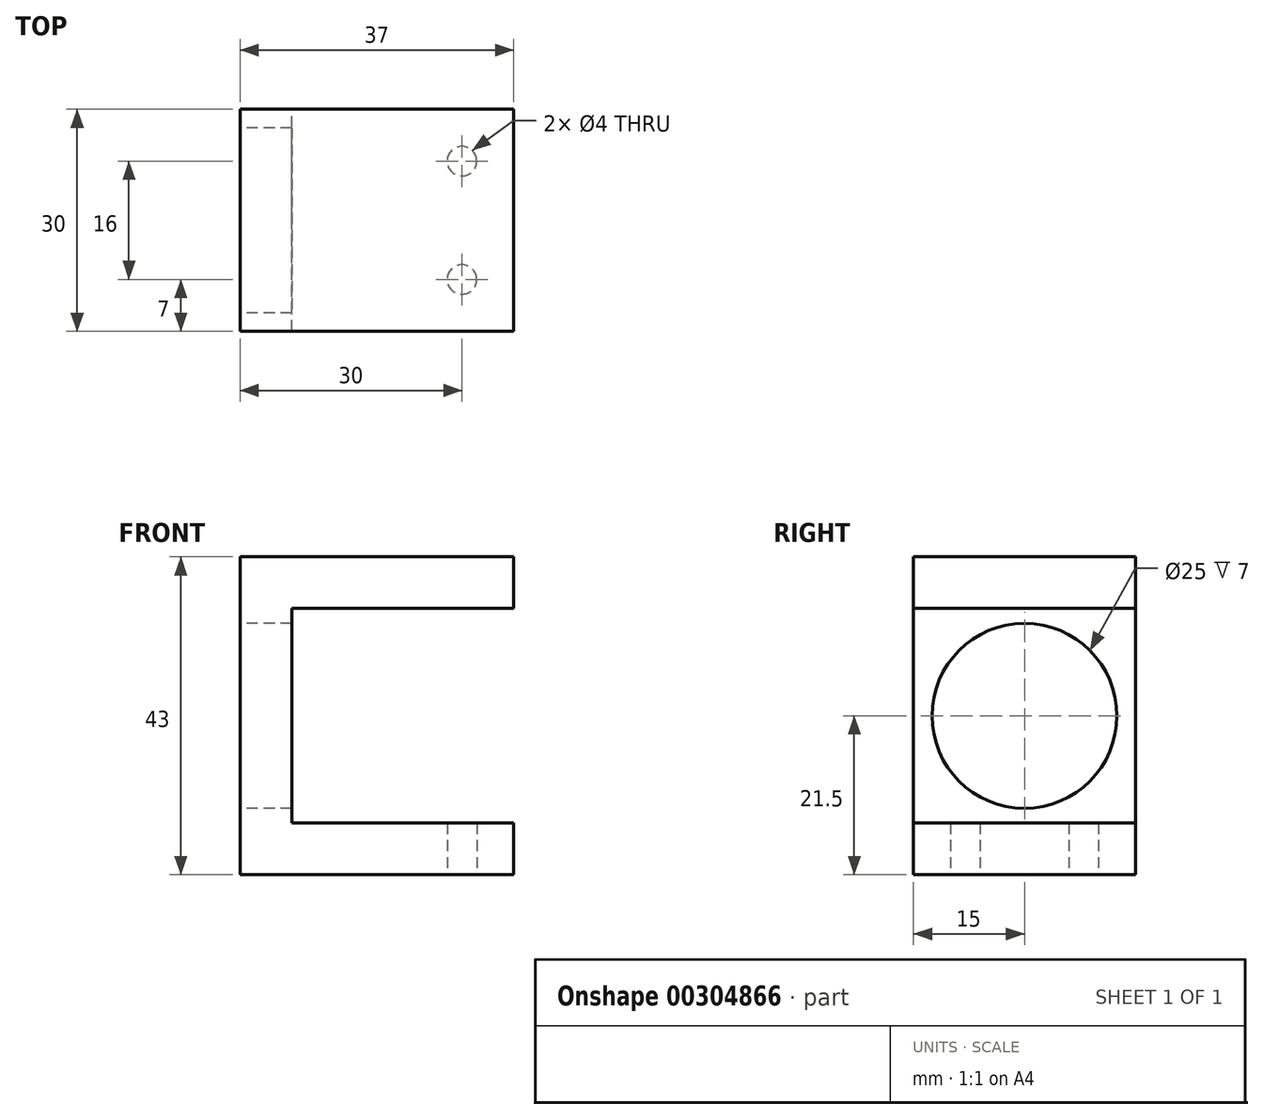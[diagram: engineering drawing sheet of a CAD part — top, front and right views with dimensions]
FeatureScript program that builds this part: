
annotation { "Feature Type Name" : "Feature", "Feature Type Description" : "" }
export const myFeature = defineFeature(function(context is Context, id is Id, definition is map)
    precondition{}
    {
        {
            var Q0;
            Q0=qCreatedBy(makeId("Front.planeOp"),FACE);
            var sketch = newSketch(context, id + "F0", { "sketchPlane" : qUnion([Q0])});
            skLineSegment(sketch, "E0.bottom", {"start": v(15, -14.5) * mm, "end": v(-15, -14.5) * mm});
            skLineSegment(sketch, "E0.top", {"start": v(15, 14.5) * mm, "end": v(-15, 14.5) * mm});
            skLineSegment(sketch, "E0.left", {"start": v(15, -14.5) * mm, "end": v(15, 14.5) * mm});
            skLineSegment(sketch, "E0.right", {"start": v(-15, -14.5) * mm, "end": v(-15, 14.5) * mm});
            skPoint(sketch, "E0.middle", {"position": v(0, 0) * mm});
            skLineSegment(sketch, "E1.0", {"start": v(22, 21.5) * mm, "end": v(-22, 21.5) * mm});
            skLineSegment(sketch, "E1.1", {"start": v(22, -21.5) * mm, "end": v(22, 21.5) * mm});
            skLineSegment(sketch, "E1.2", {"start": v(22, -21.5) * mm, "end": v(-22, -21.5) * mm});
            skLineSegment(sketch, "E1.3", {"start": v(-22, -21.5) * mm, "end": v(-22, 21.5) * mm});
            skLineSegment(sketch, "E2", {"start": v(15, 14.5) * mm, "end": v(15, 21.5) * mm});
            skLineSegment(sketch, "E3", {"start": v(15, -14.5) * mm, "end": v(15, -21.5) * mm});
            skSolve(sketch);
        }
        {
            var Q0;
            Q0=makeQuery(id+"F0.imprint","IMPRINT",FACE,{"disambiguationData":[TD([[makeQuery(id+"F0.imprint","IMPRINT",EDGE,{"derivedFrom":sQuery(id+"F0.wireOp",EDGE,"E0.bottom")}),1.0]])]});
            extrude(context, id + "F1", {"entities" : qUnion([Q0]), "depth" : 30 * mm});
        }
        {
            var Q0;
            Q0=makeQuery(id+"F1.opExtrude","SWEPT_FACE",FACE,{"disambiguationData":[OSD([sQuery(id+"F0.wireOp",EDGE,"E1.3")])]});
            var sketch = newSketch(context, id + "F2", { "sketchPlane" : qUnion([Q0])});
            skSolve(sketch);
        }
        {
            var Q0;
            Q0=makeQuery(id+"F1.opExtrude","SWEPT_FACE",FACE,{"disambiguationData":[OSD([sQuery(id+"F0.wireOp",EDGE,"E1.2")])]});
            var sketch = newSketch(context, id + "F3", { "sketchPlane" : qUnion([Q0])});
            skLineSegment(sketch, "E4", {"start": v(8, 30) * mm, "end": v(8, 0) * mm, "construction": true});
            skCircle(sketch, "E5", {"center": v(8, 23) * mm, "radius": 2 * mm});
            skLineSegment(sketch, "E6", {"start": v(-22, 15) * mm, "end": v(15, 15) * mm});
            skCircle(sketch, "E7.MirrorC", {"center": v(8, 7) * mm, "radius": 2 * mm});
            skSolve(sketch);
        }
        {
            var Q0;
            Q0 = qSketchRegion(id + "F3", true);
            var Q1;
            Q1=makeQuery(id+"F1.opExtrude","SWEPT_FACE",FACE,{"disambiguationData":[OSD([sQuery(id+"F0.wireOp",EDGE,"E0.bottom")])]});
            extrude(context, id + "F4", {"entities" : qUnion([Q0]), "operationType" : NewBodyOperationType.REMOVE, "endBound" : BoundingType.UP_TO_SURFACE, "oppositeDirection" : true, "endBoundEntityFace" : qUnion([Q1]), "depth" : 25 * mm});
        }
        {
            var Q0;
            {var subQ0=sQuery(id+"F0.wireOp",EDGE,"E1.3");Q0=makeQuery(id+"F2.imprint","IMPRINT",FACE,{"disambiguationData":[TD([[makeQuery(id+"F2.imprint","IMPRINT",EDGE,{"derivedFrom":makeQuery(id+"F1.opExtrude","CAP_EDGE",EDGE,{"disambiguationData":[OSD([subQ0])],"isStart":true})}),-1.0]])]});}
            var sketch = newSketch(context, id + "F5", { "sketchPlane" : qUnion([Q0])});
            skLineSegment(sketch, "E8.0.0", {"start": v(0, 21.5) * mm, "end": v(0, -21.5) * mm, "construction": true});
            skLineSegment(sketch, "E8.0.1", {"start": v(0, -21.5) * mm, "end": v(30, -21.5) * mm, "construction": true});
            skLineSegment(sketch, "E8.0.2", {"start": v(30, -21.5) * mm, "end": v(30, 21.5) * mm, "construction": true});
            skLineSegment(sketch, "E8.0.3", {"start": v(30, 21.5) * mm, "end": v(0, 21.5) * mm, "construction": true});
            skPoint(sketch, "E9", {"position": v(15, 0) * mm});
            skPoint(sketch, "E9.positionSnap0", {"position": v(30, 0) * mm});
            skPoint(sketch, "E9.positionSnap1", {"position": v(15, -21.5) * mm});
            skCircle(sketch, "E10", {"center": v(15, 0) * mm, "radius": 12.5 * mm});
            skSolve(sketch);
        }
        {
            var Q0;
            Q0=makeQuery(id+"F5.imprint","IMPRINT",FACE,{"disambiguationData":[TD([[makeQuery(id+"F5.imprint","IMPRINT",EDGE,{"derivedFrom":sQuery(id+"F5.wireOp",EDGE,"E10")}),1.0]])]});
            var Q1;
            Q1=makeQuery(id+"F1.opExtrude","SWEPT_FACE",FACE,{"disambiguationData":[OSD([sQuery(id+"F0.wireOp",EDGE,"E0.right")])]});
            extrude(context, id + "F6", {"entities" : qUnion([Q0]), "operationType" : NewBodyOperationType.REMOVE, "endBound" : BoundingType.UP_TO_SURFACE, "oppositeDirection" : true, "endBoundEntityFace" : qUnion([Q1]), "depth" : 25 * mm});
        }
    });
